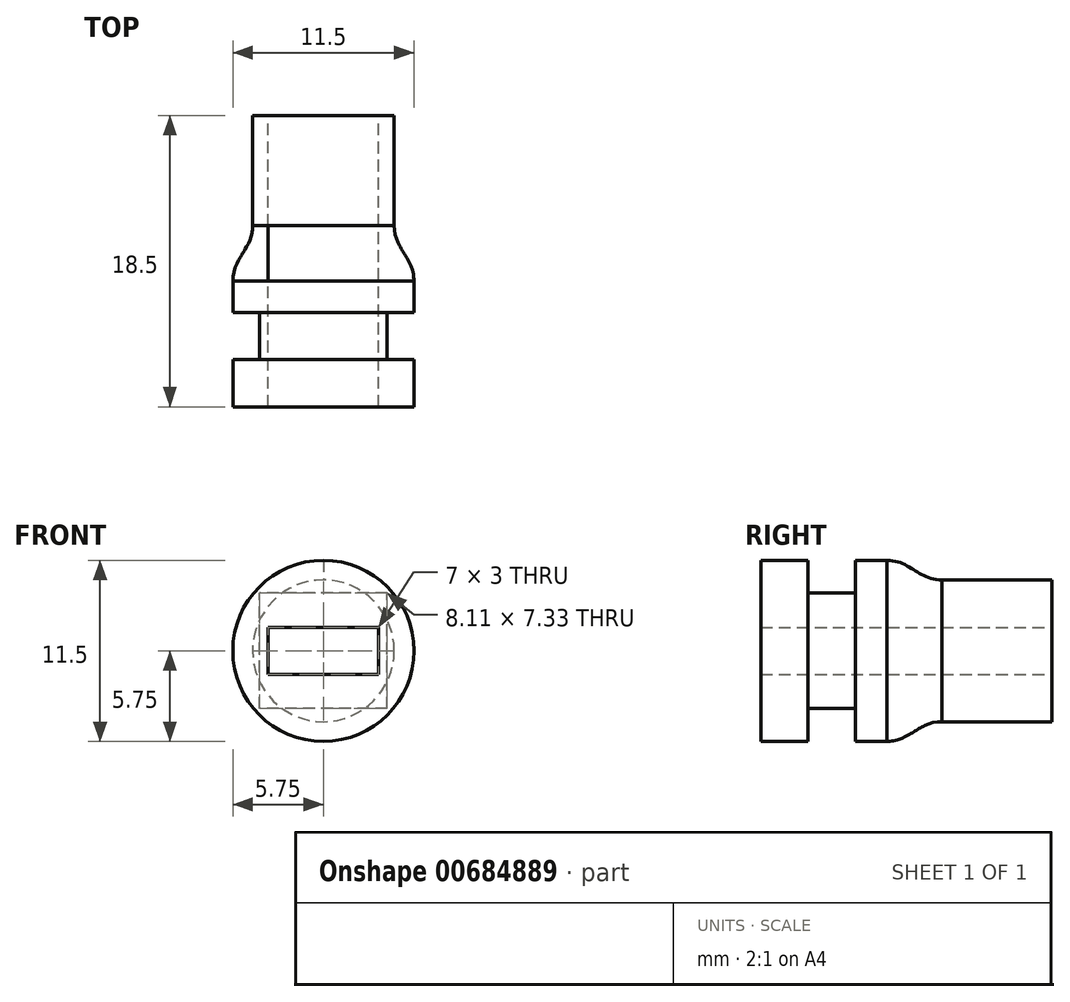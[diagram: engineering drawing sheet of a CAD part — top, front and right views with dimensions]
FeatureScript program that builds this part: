
annotation { "Feature Type Name" : "Feature", "Feature Type Description" : "" }
export const myFeature = defineFeature(function(context is Context, id is Id, definition is map)
    precondition{}
    {
        {
            var Q0;
            Q0=qCreatedBy(makeId("Top.planeOp"),FACE);
            var sketch = newSketch(context, id + "F0", { "sketchPlane" : qUnion([Q0])});
            skLineSegment(sketch, "E0.bottom", {"start": v(0, 3) * mm, "end": v(5.75, 3) * mm});
            skLineSegment(sketch, "E0.top", {"start": v(0, 0) * mm, "end": v(5.75, 0) * mm});
            skLineSegment(sketch, "E0.left", {"start": v(0, 3) * mm, "end": v(0, 0) * mm});
            skLineSegment(sketch, "E0.right", {"start": v(5.75, 3) * mm, "end": v(5.75, 0) * mm});
            skLineSegment(sketch, "E1.bottom", {"start": v(0, 18.5) * mm, "end": v(4.5, 18.5) * mm});
            skLineSegment(sketch, "E1.left", {"start": v(0, 18.5) * mm, "end": v(0, 6) * mm});
            skLineSegment(sketch, "E1.right", {"start": v(4.5, 18.5) * mm, "end": v(4.5, 11.5) * mm});
            skLineSegment(sketch, "E2", {"start": v(0, 6) * mm, "end": v(5.75, 6) * mm});
            skLineSegment(sketch, "E3", {"start": v(5.75, 6) * mm, "end": v(5.75, 8) * mm});
            skFitSpline(sketch, "E4", {"points": [v(5.75, 8) * mm, v(4.5, 11.5) * mm], "startDerivative": vector(0, 4.5) * mm, "endDerivative": vector(0, 4.5) * mm});
            skLineSegment(sketch, "E5", {"start": v(5.75, 8) * mm, "end": v(5.75, 9.5) * mm, "construction": true});
            skLineSegment(sketch, "E6", {"start": v(4.5, 10) * mm, "end": v(4.5, 11.5) * mm, "construction": true});
            skLineSegment(sketch, "E7", {"start": v(0, 51.44) * mm, "end": v(0, -36.37) * mm, "construction": true});
            skSolve(sketch);
        }
        {
            var Q0;
            Q0=makeQuery(id+"F0.imprint","IMPRINT",FACE,{"disambiguationData":[TD([[makeQuery(id+"F0.imprint","IMPRINT",EDGE,{"derivedFrom":sQuery(id+"F0.wireOp",EDGE,"E1.bottom")}),-1.0]])]});
            var Q1;
            Q1=makeQuery(id+"F0.imprint","IMPRINT",FACE,{"disambiguationData":[TD([[makeQuery(id+"F0.imprint","IMPRINT",EDGE,{"derivedFrom":sQuery(id+"F0.wireOp",EDGE,"E0.bottom")}),-1.0]])]});
            var Q2;
            Q2=sQuery(id+"F0.wireOp",EDGE,"E1.right");
            var Q3;
            Q3=sQuery(id+"F0.wireOp",EDGE,"E1.bottom");
            var Q4;
            Q4=sQuery(id+"F0.wireOp",EDGE,"E4");
            var Q5;
            Q5=sQuery(id+"F0.wireOp",EDGE,"E3");
            var Q6;
            Q6=sQuery(id+"F0.wireOp",EDGE,"E2");
            var Q7;
            Q7=sQuery(id+"F0.wireOp",EDGE,"E0.bottom");
            var Q8;
            Q8=sQuery(id+"F0.wireOp",EDGE,"E0.right");
            var Q9;
            Q9=sQuery(id+"F0.wireOp",EDGE,"E0.top");
            var Q10;
            Q10=sQuery(id+"F0.wireOp",EDGE,"E7");
            revolve(context, id + "F1", {"entities" : qUnion([Q0, Q1]), "surfaceEntities" : qUnion([Q2, Q3, Q4, Q5, Q6, Q7, Q8, Q9]), "axis" : qUnion([Q10]), "revolveType" : RevolveType.FULL});
        }
        {
            var Q0;
            Q0=makeQuery(id+"F1.opRevolve","SWEPT_FACE",FACE,{"disambiguationData":[OSD([sQuery(id+"F0.wireOp",EDGE,"E0.bottom")])]});
            var sketch = newSketch(context, id + "F2", { "sketchPlane" : qUnion([Q0])});
            skLineSegment(sketch, "E8.bottom", {"start": v(-4.26, -3.87) * mm, "end": v(4.26, -3.87) * mm, "construction": true});
            skLineSegment(sketch, "E8.top", {"start": v(-4.26, 3.87) * mm, "end": v(4.26, 3.87) * mm, "construction": true});
            skLineSegment(sketch, "E8.left", {"start": v(-4.26, -3.87) * mm, "end": v(-4.26, 3.87) * mm, "construction": true});
            skLineSegment(sketch, "E8.right", {"start": v(4.26, -3.87) * mm, "end": v(4.26, 3.87) * mm, "construction": true});
            skLineSegment(sketch, "E9.0", {"start": v(-4.06, -3.67) * mm, "end": v(4.06, -3.67) * mm});
            skLineSegment(sketch, "E9.1", {"start": v(-4.06, -3.67) * mm, "end": v(-4.06, 3.67) * mm});
            skLineSegment(sketch, "E9.2", {"start": v(-4.06, 3.67) * mm, "end": v(4.06, 3.67) * mm});
            skLineSegment(sketch, "E9.3", {"start": v(4.06, -3.67) * mm, "end": v(4.06, 3.67) * mm});
            skSolve(sketch);
        }
        {
            var Q0;
            Q0=makeQuery(id+"F2.imprint","IMPRINT",FACE,{"disambiguationData":[TD([[makeQuery(id+"F2.imprint","IMPRINT",EDGE,{"derivedFrom":sQuery(id+"F2.wireOp",EDGE,"E9.0")}),1.0]])]});
            extrude(context, id + "F3", {"entities" : qUnion([Q0]), "operationType" : NewBodyOperationType.ADD, "endBound" : BoundingType.UP_TO_NEXT, "depth" : 25 * mm, "offsetDistance" : 25 * mm});
        }
        {
            var Q0;
            Q0=makeQuery(id+"F1.opRevolve","SWEPT_FACE",FACE,{"disambiguationData":[OSD([sQuery(id+"F0.wireOp",EDGE,"E1.bottom")])]});
            var sketch = newSketch(context, id + "F4", { "sketchPlane" : qUnion([Q0])});
            skLineSegment(sketch, "E10.bottom", {"start": v(-3.5, 1.5) * mm, "end": v(3.5, 1.5) * mm});
            skLineSegment(sketch, "E10.top", {"start": v(-3.5, -1.5) * mm, "end": v(3.5, -1.5) * mm});
            skLineSegment(sketch, "E10.left", {"start": v(-3.5, 1.5) * mm, "end": v(-3.5, -1.5) * mm});
            skLineSegment(sketch, "E10.right", {"start": v(3.5, 1.5) * mm, "end": v(3.5, -1.5) * mm});
            skLineSegment(sketch, "E11", {"start": v(-3.5, -1.5) * mm, "end": v(3.5, 1.5) * mm, "construction": true});
            skLineSegment(sketch, "E12", {"start": v(-3.5, 1.5) * mm, "end": v(3.5, -1.5) * mm, "construction": true});
            skSolve(sketch);
        }
        {
            var Q0;
            Q0=makeQuery(id+"F4.imprint","IMPRINT",FACE,{"disambiguationData":[TD([[makeQuery(id+"F4.imprint","IMPRINT",EDGE,{"derivedFrom":sQuery(id+"F4.wireOp",EDGE,"E10.bottom")}),-1.0]])]});
            extrude(context, id + "F5", {"entities" : qUnion([Q0]), "operationType" : NewBodyOperationType.REMOVE, "endBound" : BoundingType.THROUGH_ALL, "oppositeDirection" : true, "depth" : 25 * mm, "offsetDistance" : 25 * mm});
        }
    });
